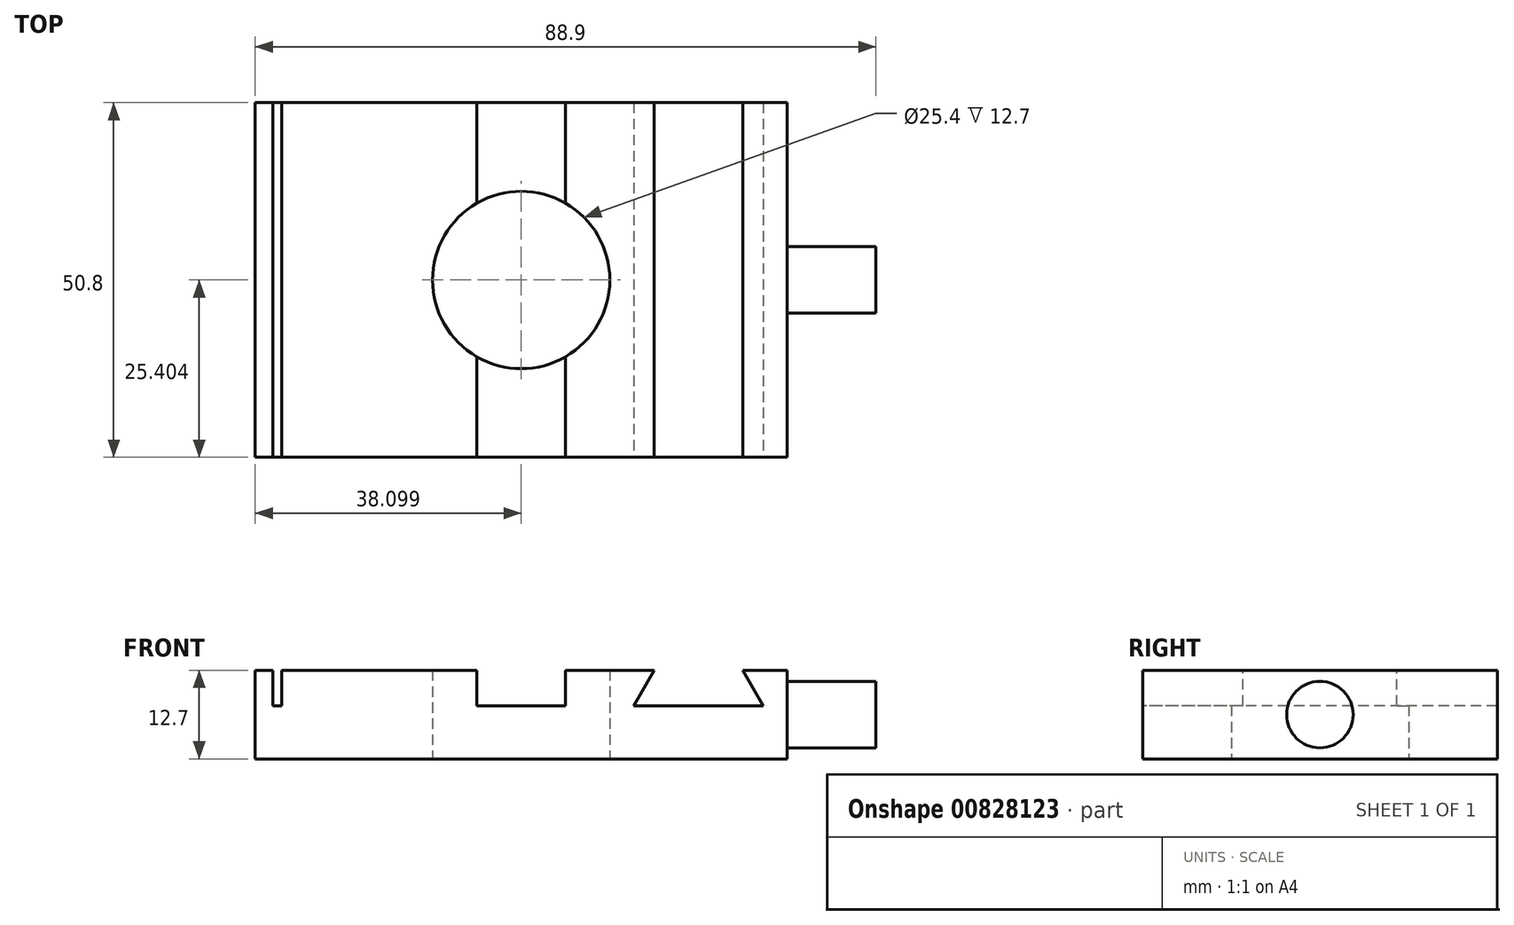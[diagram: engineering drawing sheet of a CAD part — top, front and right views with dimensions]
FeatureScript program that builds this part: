
annotation { "Feature Type Name" : "Feature", "Feature Type Description" : "" }
export const myFeature = defineFeature(function(context is Context, id is Id, definition is map)
    precondition{}
    {
        {
            var Q0;
            Q0=qCreatedBy(makeId("Top.planeOp"),FACE);
            var sketch = newSketch(context, id + "F0", { "sketchPlane" : qUnion([Q0])});
            skLineSegment(sketch, "E0.bottom", {"start": v(-30.83, 28.3) * mm, "end": v(45.37, 28.3) * mm});
            skLineSegment(sketch, "E0.top", {"start": v(-30.83, -22.5) * mm, "end": v(45.37, -22.5) * mm});
            skLineSegment(sketch, "E0.left", {"start": v(-30.83, 28.3) * mm, "end": v(-30.83, -22.5) * mm});
            skLineSegment(sketch, "E0.right", {"start": v(45.37, 28.3) * mm, "end": v(45.37, -22.5) * mm});
            skCircle(sketch, "E1", {"center": v(7.27, 2.9) * mm, "radius": 12.7 * mm});
            skPoint(sketch, "E1.centerSnap0", {"position": v(-30.83, 2.9) * mm});
            skPoint(sketch, "E1.centerSnap1", {"position": v(7.27, 28.3) * mm});
            skSolve(sketch);
        }
        {
            var Q0;
            Q0=makeQuery(id+"F0.imprint","IMPRINT",FACE,{"disambiguationData":[TD([[makeQuery(id+"F0.imprint","IMPRINT",EDGE,{"derivedFrom":sQuery(id+"F0.wireOp",EDGE,"E0.bottom")}),-1.0]])]});
            extrude(context, id + "F1", {"entities" : qUnion([Q0]), "depth" : 12.7 * mm, "offsetDistance" : 25.4 * mm});
        }
        {
            var Q0;
            Q0=makeQuery(id+"F1.opExtrude","CAP_FACE",FACE,{"disambiguationData":[OSD([sQuery(id+"F0.wireOp",EDGE,"E0.bottom"),sQuery(id+"F0.wireOp",EDGE,"E0.top"),sQuery(id+"F0.wireOp",EDGE,"E0.left"),sQuery(id+"F0.wireOp",EDGE,"E0.right"),sQuery(id+"F0.wireOp",EDGE,"E1")])],"isStart":false});
            var sketch = newSketch(context, id + "F2", { "sketchPlane" : qUnion([Q0])});
            skLineSegment(sketch, "E2.bottom", {"start": v(-28.3, 28.3) * mm, "end": v(-27.02, 28.3) * mm});
            skLineSegment(sketch, "E2.top", {"start": v(-28.3, -22.5) * mm, "end": v(-27.02, -22.5) * mm});
            skLineSegment(sketch, "E2.left", {"start": v(-28.3, 28.3) * mm, "end": v(-28.3, -22.5) * mm});
            skLineSegment(sketch, "E2.right", {"start": v(-27.02, 28.3) * mm, "end": v(-27.02, -22.5) * mm});
            skLineSegment(sketch, "E3.bottom", {"start": v(0.92, 28.3) * mm, "end": v(13.62, 28.3) * mm});
            skLineSegment(sketch, "E3.top", {"start": v(0.92, -22.5) * mm, "end": v(13.62, -22.5) * mm});
            skLineSegment(sketch, "E3.left", {"start": v(0.92, 28.3) * mm, "end": v(0.92, -22.5) * mm});
            skLineSegment(sketch, "E3.right", {"start": v(13.62, 28.3) * mm, "end": v(13.62, -22.5) * mm});
            skLineSegment(sketch, "E4", {"start": v(7.27, 28.3) * mm, "end": v(13.62, 28.3) * mm});
            skSolve(sketch);
        }
        {
            var Q0;
            {var subQ2=sQuery(id+"F2.wireOp",EDGE,"E3.bottom");Q0=makeQuery(id+"F2.imprint","IMPRINT",FACE,{"disambiguationData":[TD([[makeQuery(id+"F2.imprint","IMPRINT",EDGE,{"derivedFrom":subQ2}),-1.0]])]});}
            var Q1;
            {var subQ0=sQuery(id+"F2.wireOp",EDGE,"E3.top");Q1=makeQuery(id+"F2.imprint","IMPRINT",FACE,{"disambiguationData":[TD([[makeQuery(id+"F2.imprint","IMPRINT",EDGE,{"derivedFrom":subQ0}),1.0]])]});}
            var Q2;
            Q2=makeQuery(id+"F2.imprint","IMPRINT",FACE,{"disambiguationData":[TD([[makeQuery(id+"F2.imprint","IMPRINT",EDGE,{"derivedFrom":sQuery(id+"F2.wireOp",EDGE,"E2.bottom")}),-1.0]])]});
            extrude(context, id + "F3", {"entities" : qUnion([Q0, Q1, Q2]), "operationType" : NewBodyOperationType.REMOVE, "oppositeDirection" : true, "depth" : 5.08 * mm, "offsetDistance" : 25.4 * mm});
        }
        {
            var Q0;
            Q0=makeQuery(id+"F1.opExtrude","SWEPT_FACE",FACE,{"disambiguationData":[OSD([sQuery(id+"F0.wireOp",EDGE,"E0.top")])]});
            var sketch = newSketch(context, id + "F4", { "sketchPlane" : qUnion([Q0])});
            skLineSegment(sketch, "E5", {"start": v(26.32, 12.7) * mm, "end": v(39.02, 12.7) * mm});
            skLineSegment(sketch, "E6", {"start": v(39.02, 12.7) * mm, "end": v(41.95, 7.62) * mm});
            skLineSegment(sketch, "E7", {"start": v(41.95, 7.62) * mm, "end": v(23.39, 7.62) * mm});
            skLineSegment(sketch, "E8", {"start": v(23.39, 7.62) * mm, "end": v(26.32, 12.7) * mm});
            skLineSegment(sketch, "E9", {"start": v(7.27, 7.62) * mm, "end": v(13.62, 7.62) * mm});
            skLineSegment(sketch, "E10", {"start": v(23.39, 7.62) * mm, "end": v(32.67, 7.62) * mm});
            skSolve(sketch);
        }
        {
            var Q0;
            Q0=makeQuery(id+"F4.imprint","IMPRINT",FACE,{"disambiguationData":[TD([[makeQuery(id+"F4.imprint","IMPRINT",EDGE,{"derivedFrom":sQuery(id+"F4.wireOp",EDGE,"E5")}),-1.0]])]});
            extrude(context, id + "F5", {"entities" : qUnion([Q0]), "operationType" : NewBodyOperationType.REMOVE, "endBound" : BoundingType.THROUGH_ALL, "oppositeDirection" : true, "depth" : 25.4 * mm, "offsetDistance" : 25.4 * mm});
        }
        {
            var Q0;
            Q0=makeQuery(id+"F1.opExtrude","SWEPT_FACE",FACE,{"disambiguationData":[OSD([sQuery(id+"F0.wireOp",EDGE,"E0.right")])]});
            var sketch = newSketch(context, id + "F6", { "sketchPlane" : qUnion([Q0])});
            skCircle(sketch, "E11", {"center": v(2.9, 6.35) * mm, "radius": 4.76 * mm});
            skPoint(sketch, "E11.centerSnap0", {"position": v(-22.5, 6.35) * mm});
            skPoint(sketch, "E11.centerSnap1", {"position": v(2.9, 12.7) * mm});
            skSolve(sketch);
        }
        {
            var Q0;
            Q0=makeQuery(id+"F6.imprint","IMPRINT",FACE,{"disambiguationData":[TD([[makeQuery(id+"F6.imprint","IMPRINT",EDGE,{"derivedFrom":sQuery(id+"F6.wireOp",EDGE,"E11")}),1.0]])]});
            extrude(context, id + "F7", {"entities" : qUnion([Q0]), "operationType" : NewBodyOperationType.ADD, "depth" : 12.7 * mm, "offsetDistance" : 25.4 * mm});
        }
    });
